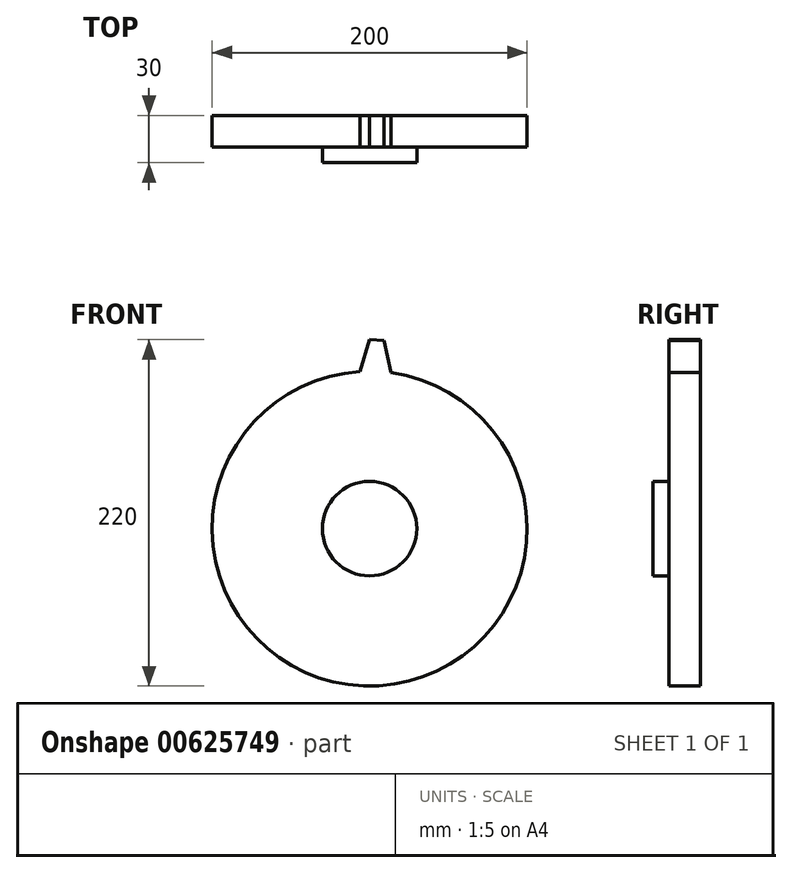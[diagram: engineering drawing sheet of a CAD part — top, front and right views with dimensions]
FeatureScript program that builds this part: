
annotation { "Feature Type Name" : "Feature", "Feature Type Description" : "" }
export const myFeature = defineFeature(function(context is Context, id is Id, definition is map)
    precondition{}
    {
        {
            var Q0;
            Q0=qCreatedBy(makeId("Front.planeOp"),FACE);
            var sketch = newSketch(context, id + "F0", { "sketchPlane" : qUnion([Q0])});
            skCircle(sketch, "E0", {"center": v(0, 0) * mm, "radius": 30 * mm});
            skCircle(sketch, "E1", {"center": v(0, 0) * mm, "radius": 100 * mm});
            skCircle(sketch, "E2", {"center": v(0, 0) * mm, "radius": 120 * mm, "construction": true});
            skLineSegment(sketch, "E3", {"start": v(-6.23, 99.8) * mm, "end": v(0, 120) * mm});
            skLineSegment(sketch, "E4", {"start": v(0, 120) * mm, "end": v(9, 119.66) * mm});
            skLineSegment(sketch, "E5", {"start": v(9, 119.66) * mm, "end": v(13.7, 99.06) * mm});
            skSolve(sketch);
        }
        {
            var Q0;
            Q0=makeQuery(id+"F0.imprint","IMPRINT",FACE,{"disambiguationData":[TD([[makeQuery(id+"F0.imprint","IMPRINT",EDGE,{"derivedFrom":sQuery(id+"F0.wireOp",EDGE,"E0")}),1.0]])]});
            extrude(context, id + "F1", {"entities" : qUnion([Q0]), "depth" : 30 * mm, "offsetDistance" : 25 * mm});
        }
        {
            var Q0;
            Q0=makeQuery(id+"F0.imprint","IMPRINT",FACE,{"disambiguationData":[TD([[makeQuery(id+"F0.imprint","IMPRINT",EDGE,{"derivedFrom":sQuery(id+"F0.wireOp",EDGE,"E0")}),-1.0]])]});
            extrude(context, id + "F2", {"entities" : qUnion([Q0]), "operationType" : NewBodyOperationType.ADD, "depth" : 20 * mm, "offsetDistance" : 25 * mm});
        }
        {
            var Q0;
            {var subQ0=sQuery(id+"F0.wireOp",EDGE,"E3");Q0=makeQuery(id+"F0.imprint","IMPRINT",FACE,{"disambiguationData":[TD([[makeQuery(id+"F0.imprint","IMPRINT",EDGE,{"derivedFrom":subQ0}),-1.0]])]});}
            extrude(context, id + "F3", {"entities" : qUnion([Q0]), "operationType" : NewBodyOperationType.ADD, "depth" : 20 * mm, "offsetDistance" : 25 * mm});
        }
    });
